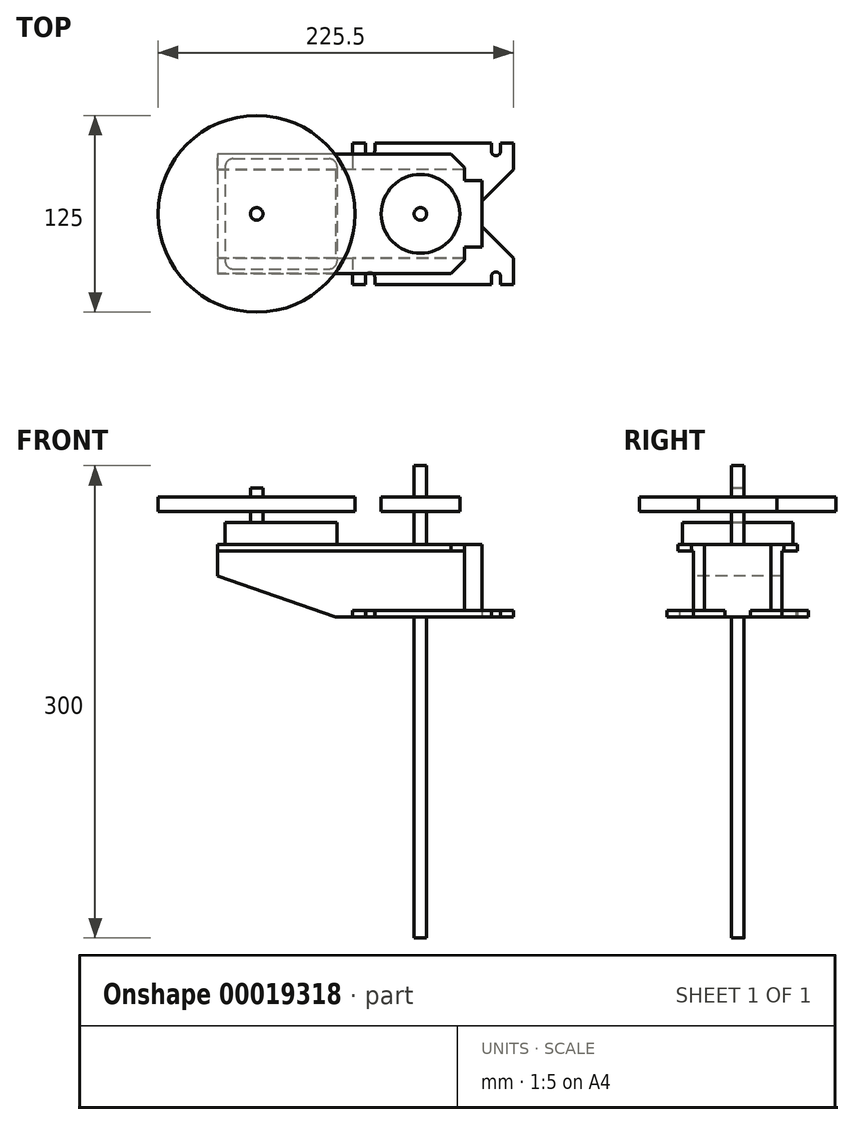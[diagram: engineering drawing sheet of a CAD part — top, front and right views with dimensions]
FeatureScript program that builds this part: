
annotation { "Feature Type Name" : "Feature", "Feature Type Description" : "" }
export const myFeature = defineFeature(function(context is Context, id is Id, definition is map)
    precondition{}
    {
        {
            var Q0;
            Q0=qCreatedBy(makeId("Top.planeOp"),FACE);
            var sketch = newSketch(context, id + "F0", { "sketchPlane" : qUnion([Q0])});
            skLineSegment(sketch, "E0.bottom", {"start": v(-78.5, 38) * mm, "end": v(78.5, 38) * mm, "construction": true});
            skLineSegment(sketch, "E0.top", {"start": v(-78.5, -38) * mm, "end": v(78.5, -38) * mm, "construction": true});
            skLineSegment(sketch, "E0.left", {"start": v(-78.5, 38) * mm, "end": v(-78.5, -38) * mm});
            skLineSegment(sketch, "E0.right", {"start": v(78.5, 38) * mm, "end": v(78.5, -38) * mm, "construction": true});
            skLineSegment(sketch, "E1", {"start": v(78.5, 0) * mm, "end": v(-78.5, 0) * mm, "construction": true});
            skLineSegment(sketch, "E2", {"start": v(0, 38) * mm, "end": v(0, -38) * mm, "construction": true});
            skLineSegment(sketch, "E3.bottom", {"start": v(78.5, 21) * mm, "end": v(89.5, 21) * mm});
            skLineSegment(sketch, "E3.top", {"start": v(78.5, -21) * mm, "end": v(89.5, -21) * mm});
            skLineSegment(sketch, "E3.left", {"start": v(78.5, 21) * mm, "end": v(78.5, -21) * mm, "construction": true});
            skLineSegment(sketch, "E3.right", {"start": v(89.5, 21) * mm, "end": v(89.5, -21) * mm});
            skLineSegment(sketch, "E4", {"start": v(78.5, 0) * mm, "end": v(89.5, 0) * mm, "construction": true});
            skLineSegment(sketch, "E5", {"start": v(78.5, 21) * mm, "end": v(78.5, 38) * mm, "construction": true});
            skLineSegment(sketch, "E6", {"start": v(78.5, -21) * mm, "end": v(78.5, -38) * mm, "construction": true});
            skLineSegment(sketch, "E7", {"start": v(78.5, 29.5) * mm, "end": v(70, 38) * mm});
            skLineSegment(sketch, "E8", {"start": v(78.5, 21) * mm, "end": v(78.5, 29.5) * mm});
            skLineSegment(sketch, "E9", {"start": v(70, 38) * mm, "end": v(-78.5, 38) * mm});
            skLineSegment(sketch, "E10", {"start": v(78.5, -29.5) * mm, "end": v(70, -38) * mm});
            skLineSegment(sketch, "E11", {"start": v(70, -38) * mm, "end": v(-78.5, -38) * mm});
            skLineSegment(sketch, "E12", {"start": v(78.5, -21) * mm, "end": v(78.5, -29.5) * mm});
            skSolve(sketch);
        }
        {
            var Q0;
            Q0=qSketchRegion(id+"F0",true);
            extrude(context, id + "F1", {"entities" : qUnion([Q0]), "depth" : 46 * mm});
        }
        {
            var Q0;
            Q0=makeQuery(id+"F1.opExtrude","SWEPT_FACE",FACE,{"disambiguationData":[OSD([sQuery(id+"F0.wireOp",EDGE,"E11")])]});
            var sketch = newSketch(context, id + "F2", { "sketchPlane" : qUnion([Q0])});
            skLineSegment(sketch, "E13", {"start": v(-78.5, 26) * mm, "end": v(-3.5, 0) * mm});
            skLineSegment(sketch, "E14", {"start": v(-78.5, 26) * mm, "end": v(-93.5, 26) * mm});
            skLineSegment(sketch, "E15", {"start": v(-93.5, 26) * mm, "end": v(-93.5, -14) * mm});
            skLineSegment(sketch, "E16", {"start": v(-93.5, -14) * mm, "end": v(-3.5, -14) * mm});
            skLineSegment(sketch, "E17", {"start": v(-3.5, -14) * mm, "end": v(-3.5, 0) * mm});
            skSolve(sketch);
        }
        {
            var Q0;
            Q0=qSketchRegion(id+"F2",true);
            extrude(context, id + "F3", {"entities" : qUnion([Q0]), "operationType" : NewBodyOperationType.REMOVE, "endBound" : BoundingType.THROUGH_ALL, "oppositeDirection" : true, "depth" : 25 * mm});
        }
        {
            var Q0;
            Q0=makeQuery(id+"F1.opExtrude","SWEPT_FACE",FACE,{"disambiguationData":[OSD([sQuery(id+"F0.wireOp",EDGE,"E11")])]});
            var sketch = newSketch(context, id + "F4", { "sketchPlane" : qUnion([Q0])});
            skLineSegment(sketch, "E18.bottom", {"start": v(-78.5, 42) * mm, "end": v(109.5, 42) * mm});
            skLineSegment(sketch, "E18.top", {"start": v(-78.5, 0) * mm, "end": v(109.5, 0) * mm});
            skLineSegment(sketch, "E18.left", {"start": v(-78.5, 42) * mm, "end": v(-78.5, 0) * mm});
            skLineSegment(sketch, "E18.right", {"start": v(109.5, 42) * mm, "end": v(109.5, 0) * mm});
            skLineSegment(sketch, "E19.bottom", {"start": v(7.5, 0) * mm, "end": v(-22.5, 0) * mm});
            skLineSegment(sketch, "E19.top", {"start": v(7.5, 0) * mm, "end": v(-22.5, 0) * mm});
            skLineSegment(sketch, "E19.left", {"start": v(7.5, 0) * mm, "end": v(7.5, 0) * mm});
            skLineSegment(sketch, "E19.right", {"start": v(-22.5, 0) * mm, "end": v(-22.5, 0) * mm});
            skSolve(sketch);
        }
        {
            var Q0;
            Q0=qSketchRegion(id+"F4",true);
            extrude(context, id + "F5", {"entities" : qUnion([Q0]), "operationType" : NewBodyOperationType.REMOVE, "oppositeDirection" : true, "depth" : 10 * mm});
        }
        {
            var Q0;
            Q0=qCreatedBy(makeId("Top.planeOp"),FACE);
            var sketch = newSketch(context, id + "F6", { "sketchPlane" : qUnion([Q0])});
            skLineSegment(sketch, "E20.bottom", {"start": v(7.5, 45) * mm, "end": v(109.5, 45) * mm});
            skLineSegment(sketch, "E20.top", {"start": v(7.5, -45) * mm, "end": v(109.5, -45) * mm});
            skLineSegment(sketch, "E20.left", {"start": v(7.5, 45) * mm, "end": v(7.5, -45) * mm});
            skLineSegment(sketch, "E20.right", {"start": v(109.5, 45) * mm, "end": v(109.5, -45) * mm, "construction": true});
            skLineSegment(sketch, "E21", {"start": v(109.5, 0) * mm, "end": v(7.5, 0) * mm, "construction": true});
            skLineSegment(sketch, "E22", {"start": v(109.5, 28) * mm, "end": v(89.5, 8) * mm});
            skLineSegment(sketch, "E23", {"start": v(89.5, 8) * mm, "end": v(89.5, 0) * mm});
            skLineSegment(sketch, "E24.0.MirrorCS", {"start": v(109.5, -28) * mm, "end": v(89.5, -8) * mm});
            skLineSegment(sketch, "E24.1.MirrorCS", {"start": v(89.5, -8) * mm, "end": v(89.5, 0) * mm});
            skLineSegment(sketch, "E25", {"start": v(109.5, 45) * mm, "end": v(109.5, 28) * mm});
            skLineSegment(sketch, "E26", {"start": v(109.5, -28) * mm, "end": v(109.5, -45) * mm});
            skCircle(sketch, "E27", {"center": v(98.5, -40) * mm, "radius": 3 * mm});
            skCircle(sketch, "E28.0.MirrorC", {"center": v(98.5, 40) * mm, "radius": 3 * mm});
            skLineSegment(sketch, "E29.bottom", {"start": v(95.5, -40) * mm, "end": v(101.5, -40) * mm});
            skLineSegment(sketch, "E29.top", {"start": v(95.5, -45) * mm, "end": v(101.5, -45) * mm});
            skLineSegment(sketch, "E29.left", {"start": v(95.5, -40) * mm, "end": v(95.5, -45) * mm});
            skLineSegment(sketch, "E29.right", {"start": v(101.5, -40) * mm, "end": v(101.5, -45) * mm});
            skLineSegment(sketch, "E30.0.MirrorCS", {"start": v(101.5, 40) * mm, "end": v(101.5, 45) * mm});
            skLineSegment(sketch, "E31.0.MirrorCS", {"start": v(95.5, 40) * mm, "end": v(95.5, 45) * mm});
            skLineSegment(sketch, "E32.0.MirrorCS", {"start": v(95.5, 40) * mm, "end": v(101.5, 40) * mm});
            skLineSegment(sketch, "E33.0.MirrorCS", {"start": v(95.5, 45) * mm, "end": v(101.5, 45) * mm});
            skLineSegment(sketch, "E34", {"start": v(58.5, -45) * mm, "end": v(58.5, 45) * mm, "construction": true});
            skLineSegment(sketch, "E35.0.MirrorCS", {"start": v(21.5, -40) * mm, "end": v(21.5, -45) * mm});
            skLineSegment(sketch, "E36.0.MirrorCS", {"start": v(15.5, -40) * mm, "end": v(15.5, -45) * mm});
            skCircle(sketch, "E37.0.MirrorC", {"center": v(18.5, -40) * mm, "radius": 3 * mm});
            skLineSegment(sketch, "E38.0.MirrorCS", {"start": v(21.5, -40) * mm, "end": v(15.5, -40) * mm});
            skCircle(sketch, "E39.0.MirrorC", {"center": v(18.5, 40) * mm, "radius": 3 * mm});
            skLineSegment(sketch, "E40.0.MirrorCS", {"start": v(21.5, 40) * mm, "end": v(15.5, 40) * mm});
            skLineSegment(sketch, "E41.0.MirrorCS", {"start": v(15.5, 40) * mm, "end": v(15.5, 45) * mm});
            skLineSegment(sketch, "E42.0.MirrorCS", {"start": v(21.5, 40) * mm, "end": v(21.5, 45) * mm});
            skSolve(sketch);
        }
        {
            var Q0;
            {var subQ6=sQuery(id+"F6.wireOp",EDGE,"E20.left");Q0=makeQuery(id+"F6.imprint","IMPRINT",FACE,{"disambiguationData":[TD([[makeQuery(id+"F6.imprint","IMPRINT",EDGE,{"derivedFrom":subQ6}),1.0]])]});}
            extrude(context, id + "F7", {"entities" : qUnion([Q0]), "operationType" : NewBodyOperationType.ADD, "depth" : 4 * mm});
        }
        {
            var Q0;
            Q0=makeQuery(id+"F1.opExtrude","SWEPT_FACE",FACE,{"disambiguationData":[OSD([sQuery(id+"F0.wireOp",EDGE,"E9")])]});
            var sketch = newSketch(context, id + "F8", { "sketchPlane" : qUnion([Q0])});
            skLineSegment(sketch, "E43.bottom", {"start": v(-109.5, 4) * mm, "end": v(78.5, 4) * mm});
            skLineSegment(sketch, "E43.top", {"start": v(-109.5, 42) * mm, "end": v(78.5, 42) * mm});
            skLineSegment(sketch, "E43.left", {"start": v(-109.5, 4) * mm, "end": v(-109.5, 42) * mm});
            skLineSegment(sketch, "E43.right", {"start": v(78.5, 4) * mm, "end": v(78.5, 42) * mm});
            skLineSegment(sketch, "E44.bottom", {"start": v(-7.5, 4) * mm, "end": v(22.5, 4) * mm});
            skLineSegment(sketch, "E44.top", {"start": v(-7.5, 0) * mm, "end": v(22.5, 0) * mm});
            skLineSegment(sketch, "E44.left", {"start": v(-7.5, 4) * mm, "end": v(-7.5, 0) * mm});
            skLineSegment(sketch, "E44.right", {"start": v(22.5, 4) * mm, "end": v(22.5, 0) * mm});
            skSolve(sketch);
        }
        {
            var Q0;
            Q0=qSketchRegion(id+"F8",true);
            extrude(context, id + "F9", {"entities" : qUnion([Q0]), "operationType" : NewBodyOperationType.REMOVE, "oppositeDirection" : true, "depth" : 10 * mm});
        }
        {
            var Q0;
            Q0=makeQuery(id+"F1.opExtrude","CAP_FACE",FACE,{"disambiguationData":[OSD([sQuery(id+"F0.wireOp",EDGE,"E0.left"),sQuery(id+"F0.wireOp",EDGE,"E3.bottom"),sQuery(id+"F0.wireOp",EDGE,"E3.top"),sQuery(id+"F0.wireOp",EDGE,"E3.right"),sQuery(id+"F0.wireOp",EDGE,"E7"),sQuery(id+"F0.wireOp",EDGE,"E8"),sQuery(id+"F0.wireOp",EDGE,"E9"),sQuery(id+"F0.wireOp",EDGE,"E10"),sQuery(id+"F0.wireOp",EDGE,"E11"),sQuery(id+"F0.wireOp",EDGE,"E12")])],"isStart":false});
            var sketch = newSketch(context, id + "F10", { "sketchPlane" : qUnion([Q0])});
            skCircle(sketch, "E45", {"center": v(50.5, 0) * mm, "radius": 4 * mm});
            skSolve(sketch);
        }
        {
            var Q0;
            Q0=qSketchRegion(id+"F10",true);
            var Q1;
            Q1=sQuery(id+"F10.wireOp",EDGE,"E45");
            extrude(context, id + "F11", {"entities" : qUnion([Q0]), "operationType" : NewBodyOperationType.ADD, "surfaceEntities" : qUnion([Q1]), "depth" : 50 * mm, "hasSecondDirection" : true, "secondDirectionOppositeDirection" : true, "secondDirectionDepth" : 250 * mm});
        }
        {
            var Q0;
            Q0=makeQuery(id+"F1.opExtrude","CAP_FACE",FACE,{"disambiguationData":[OSD([sQuery(id+"F0.wireOp",EDGE,"E0.left"),sQuery(id+"F0.wireOp",EDGE,"E3.bottom"),sQuery(id+"F0.wireOp",EDGE,"E3.top"),sQuery(id+"F0.wireOp",EDGE,"E3.right"),sQuery(id+"F0.wireOp",EDGE,"E7"),sQuery(id+"F0.wireOp",EDGE,"E8"),sQuery(id+"F0.wireOp",EDGE,"E9"),sQuery(id+"F0.wireOp",EDGE,"E10"),sQuery(id+"F0.wireOp",EDGE,"E11"),sQuery(id+"F0.wireOp",EDGE,"E12")])],"isStart":false});
            cPlane(context, id + "F12", {"entities" : qUnion([Q0]), "cplaneType" : CPlaneType.OFFSET, "offset" : 21 * mm, "width" : 150 * mm, "height" : 150 * mm});
        }
        {
            var Q0;
            Q0=qCreatedBy(id+"F12.planeOp",FACE);
            var sketch = newSketch(context, id + "F13", { "sketchPlane" : qUnion([Q0])});
            skCircle(sketch, "E46", {"center": v(50.5, 0) * mm, "radius": 25 * mm});
            skSolve(sketch);
        }
        {
            var Q0;
            Q0=qSketchRegion(id+"F13",true);
            extrude(context, id + "F14", {"entities" : qUnion([Q0]), "operationType" : NewBodyOperationType.ADD, "depth" : 9 * mm});
        }
        {
            var Q0;
            Q0=makeQuery(id+"F1.opExtrude","CAP_FACE",FACE,{"disambiguationData":[OSD([sQuery(id+"F0.wireOp",EDGE,"E0.left"),sQuery(id+"F0.wireOp",EDGE,"E3.bottom"),sQuery(id+"F0.wireOp",EDGE,"E3.top"),sQuery(id+"F0.wireOp",EDGE,"E3.right"),sQuery(id+"F0.wireOp",EDGE,"E7"),sQuery(id+"F0.wireOp",EDGE,"E8"),sQuery(id+"F0.wireOp",EDGE,"E9"),sQuery(id+"F0.wireOp",EDGE,"E10"),sQuery(id+"F0.wireOp",EDGE,"E11"),sQuery(id+"F0.wireOp",EDGE,"E12")])],"isStart":false});
            var sketch = newSketch(context, id + "F15", { "sketchPlane" : qUnion([Q0])});
            skLineSegment(sketch, "E47.bottom", {"start": v(-73.5, 35) * mm, "end": v(-2.5, 35) * mm});
            skLineSegment(sketch, "E47.top", {"start": v(-73.5, -35) * mm, "end": v(-2.5, -35) * mm});
            skLineSegment(sketch, "E47.left", {"start": v(-73.5, 35) * mm, "end": v(-73.5, -35) * mm});
            skLineSegment(sketch, "E47.right", {"start": v(-2.5, 35) * mm, "end": v(-2.5, -35) * mm});
            skSolve(sketch);
        }
        {
            var Q0;
            Q0=qSketchRegion(id+"F15",true);
            extrude(context, id + "F16", {"entities" : qUnion([Q0]), "depth" : 14 * mm});
        }
        {
            var Q0;
            Q0=makeQuery(id+"F16.opExtrude","SWEPT_EDGE",EDGE,{"disambiguationData":[OSD([sQuery(id+"F15.wireOp",EDGE,"E47.top"),sQuery(id+"F15.wireOp",EDGE,"E47.right")])]});
            var Q1;
            Q1=makeQuery(id+"F16.opExtrude","SWEPT_EDGE",EDGE,{"disambiguationData":[OSD([sQuery(id+"F15.wireOp",EDGE,"E47.top"),sQuery(id+"F15.wireOp",EDGE,"E47.left")])]});
            var Q2;
            Q2=makeQuery(id+"F16.opExtrude","SWEPT_EDGE",EDGE,{"disambiguationData":[OSD([sQuery(id+"F15.wireOp",EDGE,"E47.bottom"),sQuery(id+"F15.wireOp",EDGE,"E47.right")])]});
            var Q3;
            Q3=makeQuery(id+"F16.opExtrude","SWEPT_EDGE",EDGE,{"disambiguationData":[OSD([sQuery(id+"F15.wireOp",EDGE,"E47.bottom"),sQuery(id+"F15.wireOp",EDGE,"E47.left")])]});
            fillet(context, id + "F17", {"entities" : qUnion([Q0, Q1, Q2, Q3]), "radius" : 5 * mm, "tangentPropagation" : true, "allowEdgeOverflow" : false});
        }
        {
            var Q0;
            Q0=makeQuery(id+"F16.opExtrude","CAP_FACE",FACE,{"disambiguationData":[OSD([sQuery(id+"F15.wireOp",EDGE,"E47.bottom"),sQuery(id+"F15.wireOp",EDGE,"E47.top"),sQuery(id+"F15.wireOp",EDGE,"E47.left"),sQuery(id+"F15.wireOp",EDGE,"E47.right")])],"isStart":false});
            var sketch = newSketch(context, id + "F18", { "sketchPlane" : qUnion([Q0])});
            skCircle(sketch, "E48", {"center": v(-53.5, 0) * mm, "radius": 4 * mm});
            skSolve(sketch);
        }
        {
            var Q0;
            Q0=qSketchRegion(id+"F18",true);
            var Q1;
            Q1=sQuery(id+"F18.wireOp",EDGE,"E48");
            extrude(context, id + "F19", {"entities" : qUnion([Q0]), "operationType" : NewBodyOperationType.ADD, "surfaceEntities" : qUnion([Q1]), "depth" : 22 * mm});
        }
        {
            var Q0;
            Q0=qCreatedBy(id+"F12.planeOp",FACE);
            var sketch = newSketch(context, id + "F20", { "sketchPlane" : qUnion([Q0])});
            skCircle(sketch, "E49", {"center": v(-53.5, 0) * mm, "radius": 62.5 * mm});
            skSolve(sketch);
        }
        {
            var Q0;
            Q0=qSketchRegion(id+"F20",true);
            extrude(context, id + "F21", {"entities" : qUnion([Q0]), "operationType" : NewBodyOperationType.ADD, "depth" : 9 * mm});
        }
    });
